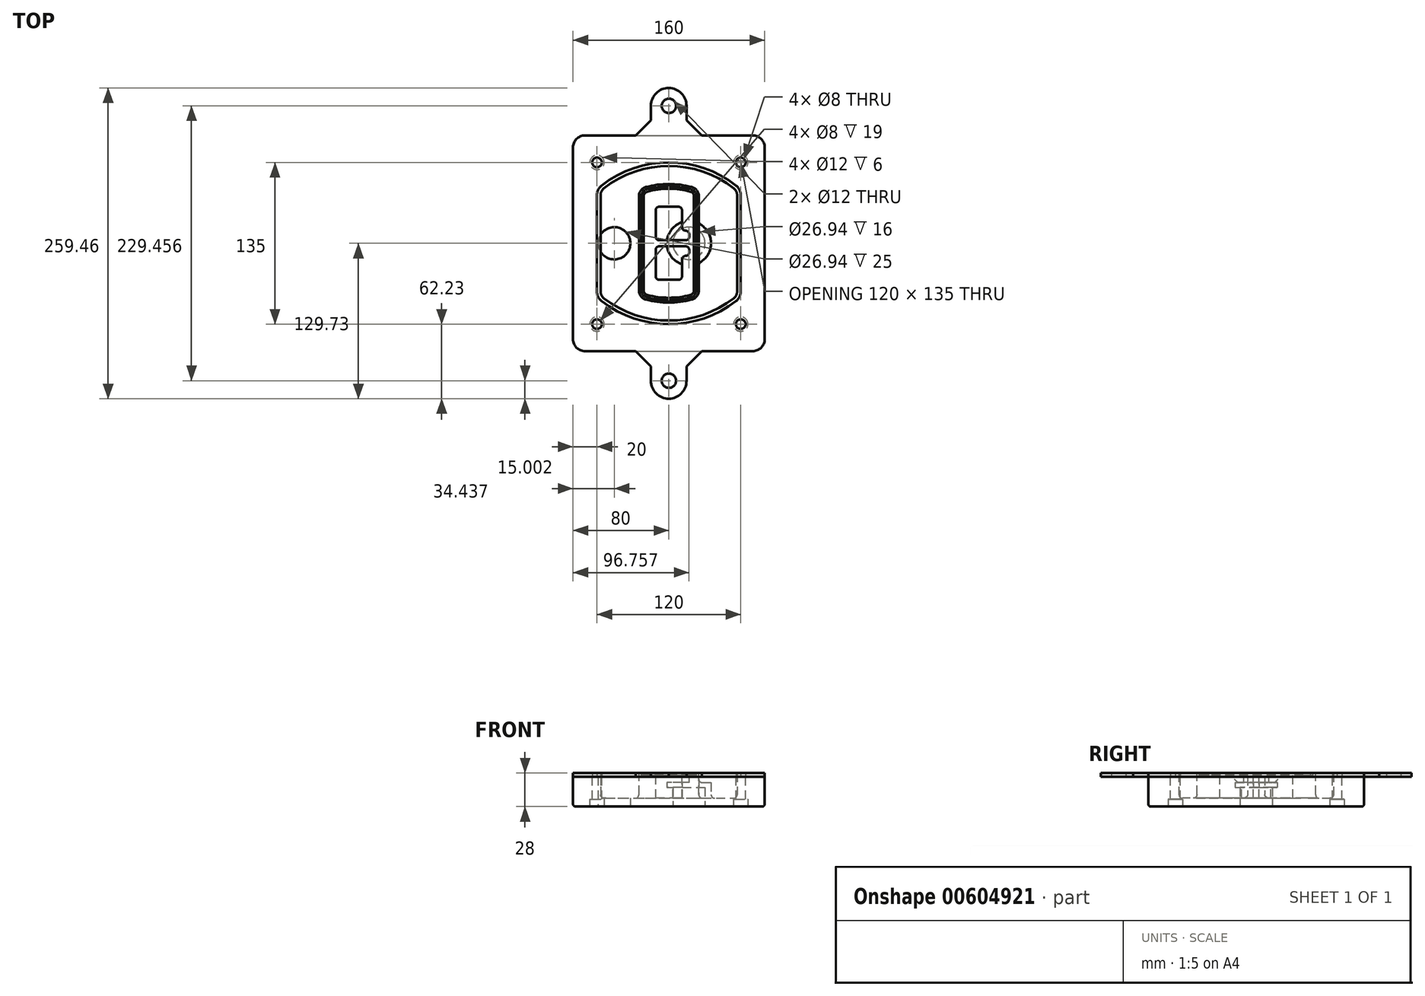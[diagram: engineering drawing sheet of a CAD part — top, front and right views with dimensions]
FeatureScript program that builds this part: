
annotation { "Feature Type Name" : "Feature", "Feature Type Description" : "" }
export const myFeature = defineFeature(function(context is Context, id is Id, definition is map)
    precondition{}
    {
        {
            var Q0;
            Q0=qCreatedBy(makeId("Top.planeOp"),FACE);
            var sketch = newSketch(context, id + "F0", { "sketchPlane" : qUnion([Q0])});
            skPoint(sketch, "E0.rect.middle", {"position": v(0, 0) * mm});
            skLineSegment(sketch, "E1.bottom", {"start": v(-70, -90) * mm, "end": v(70, -90) * mm});
            skLineSegment(sketch, "E1.top", {"start": v(-70, 90) * mm, "end": v(70, 90) * mm});
            skLineSegment(sketch, "E1.left", {"start": v(-80, -80) * mm, "end": v(-80, 80) * mm});
            skLineSegment(sketch, "E1.right", {"start": v(80, -80) * mm, "end": v(80, 80) * mm});
            skLineSegment(sketch, "E2", {"start": v(-80, 90) * mm, "end": v(80, -90) * mm, "construction": true});
            skLineSegment(sketch, "E3", {"start": v(80, 90) * mm, "end": v(-80, -90) * mm, "construction": true});
            skCircle(sketch, "E4", {"center": v(-60, 67.5) * mm, "radius": 4 * mm});
            skCircle(sketch, "E5", {"center": v(60, 67.5) * mm, "radius": 4 * mm});
            skCircle(sketch, "E6", {"center": v(60, -67.5) * mm, "radius": 4 * mm});
            skCircle(sketch, "E7", {"center": v(-60, -67.5) * mm, "radius": 4 * mm});
            skLineSegment(sketch, "E8", {"start": v(-60, 67.5) * mm, "end": v(60, 67.5) * mm, "construction": true});
            skLineSegment(sketch, "E9", {"start": v(60, 67.5) * mm, "end": v(60, -67.5) * mm, "construction": true});
            skLineSegment(sketch, "E10", {"start": v(60, -67.5) * mm, "end": v(-60, -67.5) * mm, "construction": true});
            skLineSegment(sketch, "E11", {"start": v(-60, -67.5) * mm, "end": v(-60, 67.5) * mm, "construction": true});
            skLineSegment(sketch, "E12", {"start": v(-60, 40.3) * mm, "end": v(-60, -40.3) * mm});
            skLineSegment(sketch, "E13", {"start": v(60, 40.3) * mm, "end": v(60, -40.3) * mm});
            skArc(sketch, "E14", {"start": v(56.15, 48.18) * mm, "mid": v(0, 67.5) * mm, "end": v(-56.15, 48.18) * mm});
            skArc(sketch, "E15", {"start": v(-56.15, -48.18) * mm, "mid": v(0, -67.5) * mm, "end": v(56.15, -48.18) * mm});
            skLineSegment(sketch, "E16", {"start": v(-60, 0) * mm, "end": v(60, 0) * mm, "construction": true});
            skPoint(sketch, "E17.visualSharp", {"position": v(-60, -45) * mm});
            skArc(sketch, "E17.filletArc", {"start": v(-60, -40.3) * mm, "mid": v(-58.99, -44.68) * mm, "end": v(-56.15, -48.18) * mm});
            skPoint(sketch, "E18.visualSharp", {"position": v(-60, 45) * mm});
            skArc(sketch, "E18.filletArc", {"start": v(-56.15, 48.18) * mm, "mid": v(-58.99, 44.68) * mm, "end": v(-60, 40.3) * mm});
            skPoint(sketch, "E19.visualSharp", {"position": v(60, 45) * mm});
            skArc(sketch, "E19.filletArc", {"start": v(60, 40.3) * mm, "mid": v(58.99, 44.68) * mm, "end": v(56.15, 48.18) * mm});
            skPoint(sketch, "E20.visualSharp", {"position": v(60, -45) * mm});
            skArc(sketch, "E20.filletArc", {"start": v(56.15, -48.18) * mm, "mid": v(58.99, -44.68) * mm, "end": v(60, -40.3) * mm});
            skPoint(sketch, "E21.visualSharp", {"position": v(-80, 90) * mm});
            skArc(sketch, "E21.filletArc", {"start": v(-70, 90) * mm, "mid": v(-77.07, 87.07) * mm, "end": v(-80, 80) * mm});
            skPoint(sketch, "E22.visualSharp", {"position": v(80, 90) * mm});
            skArc(sketch, "E22.filletArc", {"start": v(80, 80) * mm, "mid": v(77.07, 87.07) * mm, "end": v(70, 90) * mm});
            skPoint(sketch, "E23.visualSharp", {"position": v(80, -90) * mm});
            skArc(sketch, "E23.filletArc", {"start": v(70, -90) * mm, "mid": v(77.07, -87.07) * mm, "end": v(80, -80) * mm});
            skPoint(sketch, "E24.visualSharp", {"position": v(-80, -90) * mm});
            skArc(sketch, "E24.filletArc", {"start": v(-80, -80) * mm, "mid": v(-77.07, -87.07) * mm, "end": v(-70, -90) * mm});
            skArc(sketch, "E25.0", {"start": v(57, 40.3) * mm, "mid": v(56.3, 43.36) * mm, "end": v(54.3, 45.81) * mm});
            skLineSegment(sketch, "E25.1", {"start": v(57, 40.3) * mm, "end": v(57, -40.3) * mm});
            skArc(sketch, "E25.2", {"start": v(54.3, -45.81) * mm, "mid": v(56.3, -43.36) * mm, "end": v(57, -40.3) * mm});
            skArc(sketch, "E25.3", {"start": v(-54.3, -45.81) * mm, "mid": v(0, -64.5) * mm, "end": v(54.3, -45.81) * mm});
            skArc(sketch, "E25.4", {"start": v(-57, -40.3) * mm, "mid": v(-56.3, -43.36) * mm, "end": v(-54.3, -45.81) * mm});
            skArc(sketch, "E25.5", {"start": v(54.3, 45.81) * mm, "mid": v(0, 64.5) * mm, "end": v(-54.3, 45.81) * mm});
            skLineSegment(sketch, "E25.6", {"start": v(-57, 40.3) * mm, "end": v(-57, -40.3) * mm});
            skArc(sketch, "E25.7", {"start": v(-54.3, 45.81) * mm, "mid": v(-56.3, 43.36) * mm, "end": v(-57, 40.3) * mm});
            skArc(sketch, "E26.0", {"start": v(-58.62, 51.33) * mm, "mid": v(-62.58, 46.43) * mm, "end": v(-64, 40.3) * mm});
            skArc(sketch, "E26.1", {"start": v(58.62, 51.33) * mm, "mid": v(0, 71.5) * mm, "end": v(-58.62, 51.33) * mm});
            skArc(sketch, "E26.2", {"start": v(64, 40.3) * mm, "mid": v(62.58, 46.43) * mm, "end": v(58.62, 51.33) * mm});
            skLineSegment(sketch, "E26.3", {"start": v(64, 40.3) * mm, "end": v(64, -40.3) * mm});
            skArc(sketch, "E26.4", {"start": v(58.62, -51.33) * mm, "mid": v(62.58, -46.43) * mm, "end": v(64, -40.3) * mm});
            skLineSegment(sketch, "E26.5", {"start": v(-64, 40.3) * mm, "end": v(-64, -40.3) * mm});
            skArc(sketch, "E26.6", {"start": v(-58.62, -51.33) * mm, "mid": v(0, -71.5) * mm, "end": v(58.62, -51.33) * mm});
            skArc(sketch, "E26.7", {"start": v(-64, -40.3) * mm, "mid": v(-62.58, -46.43) * mm, "end": v(-58.62, -51.33) * mm});
            skSolve(sketch);
        }
        {
            var Q0;
            Q0=makeQuery(id+"F0.imprint","IMPRINT",FACE,{"disambiguationData":[TD([[makeQuery(id+"F0.imprint","IMPRINT",EDGE,{"derivedFrom":sQuery(id+"F0.wireOp",EDGE,"E1.bottom")}),1.0]])]});
            var Q1;
            Q1=makeQuery(id+"F0.imprint","IMPRINT",FACE,{"disambiguationData":[TD([[makeQuery(id+"F0.imprint","IMPRINT",EDGE,{"derivedFrom":sQuery(id+"F0.wireOp",EDGE,"E12")}),1.0]])]});
            var Q2;
            Q2=makeQuery(id+"F0.imprint","IMPRINT",FACE,{"disambiguationData":[TD([[makeQuery(id+"F0.imprint","IMPRINT",EDGE,{"derivedFrom":sQuery(id+"F0.wireOp",EDGE,"E25.0")}),1.0]])]});
            var Q3;
            Q3=makeQuery(id+"F0.imprint","IMPRINT",FACE,{"disambiguationData":[TD([[makeQuery(id+"F0.imprint","IMPRINT",EDGE,{"derivedFrom":sQuery(id+"F0.wireOp",EDGE,"E12")}),-1.0]])]});
            extrude(context, id + "F1", {"entities" : qUnion([Q0, Q1, Q2, Q3]), "oppositeDirection" : true, "depth" : 25 * mm});
        }
        {
            var Q0;
            Q0=makeQuery(id+"F0.imprint","IMPRINT",FACE,{"disambiguationData":[TD([[makeQuery(id+"F0.imprint","IMPRINT",EDGE,{"derivedFrom":sQuery(id+"F0.wireOp",EDGE,"E12")}),1.0]])]});
            extrude(context, id + "F2", {"entities" : qUnion([Q0]), "operationType" : NewBodyOperationType.ADD, "depth" : 3 * mm});
        }
        {
            var Q0;
            Q0=makeQuery(id+"F0.imprint","IMPRINT",FACE,{"disambiguationData":[TD([[makeQuery(id+"F0.imprint","IMPRINT",EDGE,{"derivedFrom":sQuery(id+"F0.wireOp",EDGE,"E25.0")}),1.0]])]});
            extrude(context, id + "F3", {"entities" : qUnion([Q0]), "operationType" : NewBodyOperationType.REMOVE, "oppositeDirection" : true, "depth" : 18 * mm});
        }
        {
            var Q0;
            Q0=makeQuery(id+"F2.opExtrude","CAP_FACE",FACE,{"disambiguationData":[OSD([sQuery(id+"F0.wireOp",EDGE,"E12"),sQuery(id+"F0.wireOp",EDGE,"E13"),sQuery(id+"F0.wireOp",EDGE,"E14"),sQuery(id+"F0.wireOp",EDGE,"E15"),sQuery(id+"F0.wireOp",EDGE,"E17.filletArc"),sQuery(id+"F0.wireOp",EDGE,"E18.filletArc"),sQuery(id+"F0.wireOp",EDGE,"E19.filletArc"),sQuery(id+"F0.wireOp",EDGE,"E20.filletArc"),sQuery(id+"F0.wireOp",EDGE,"E25.0"),sQuery(id+"F0.wireOp",EDGE,"E25.1"),sQuery(id+"F0.wireOp",EDGE,"E25.2"),sQuery(id+"F0.wireOp",EDGE,"E25.3"),sQuery(id+"F0.wireOp",EDGE,"E25.4"),sQuery(id+"F0.wireOp",EDGE,"E25.5"),sQuery(id+"F0.wireOp",EDGE,"E25.6"),sQuery(id+"F0.wireOp",EDGE,"E25.7")])],"isStart":false});
            var sketch = newSketch(context, id + "F4", { "sketchPlane" : qUnion([Q0])});
            skArc(sketch, "E27.0", {"start": v(-19.08, -46.97) * mm, "mid": v(0, -49.5) * mm, "end": v(19.08, -46.97) * mm});
            skArc(sketch, "E28.0", {"start": v(19.08, 46.97) * mm, "mid": v(0, 49.5) * mm, "end": v(-19.08, 46.97) * mm});
            skLineSegment(sketch, "E29", {"start": v(-25, 39.25) * mm, "end": v(-25, -39.25) * mm});
            skLineSegment(sketch, "E30", {"start": v(25, 39.25) * mm, "end": v(25, -39.25) * mm});
            skLineSegment(sketch, "E31", {"start": v(-25, 45.1) * mm, "end": v(25, 45.1) * mm, "construction": true});
            skLineSegment(sketch, "E32", {"start": v(-25, -45.1) * mm, "end": v(25, -45.1) * mm, "construction": true});
            skPoint(sketch, "E33.visualSharp", {"position": v(-25, 45.1) * mm});
            skArc(sketch, "E33.filletArc", {"start": v(-19.08, 46.97) * mm, "mid": v(-23.35, 44.11) * mm, "end": v(-25, 39.25) * mm});
            skPoint(sketch, "E34.visualSharp", {"position": v(25, 45.1) * mm});
            skArc(sketch, "E34.filletArc", {"start": v(25, 39.25) * mm, "mid": v(23.35, 44.11) * mm, "end": v(19.08, 46.97) * mm});
            skPoint(sketch, "E35.visualSharp", {"position": v(25, -45.1) * mm});
            skArc(sketch, "E35.filletArc", {"start": v(19.08, -46.97) * mm, "mid": v(23.35, -44.11) * mm, "end": v(25, -39.25) * mm});
            skPoint(sketch, "E36.visualSharp", {"position": v(-25, -45.1) * mm});
            skArc(sketch, "E36.filletArc", {"start": v(-25, -39.25) * mm, "mid": v(-23.35, -44.11) * mm, "end": v(-19.08, -46.97) * mm});
            skArc(sketch, "E37.0", {"start": v(54.3, 45.81) * mm, "mid": v(0, 64.5) * mm, "end": v(-54.3, 45.81) * mm});
            skArc(sketch, "E37.1", {"start": v(-54.3, 45.81) * mm, "mid": v(-56.3, 43.36) * mm, "end": v(-57, 40.3) * mm});
            skLineSegment(sketch, "E37.2", {"start": v(-57, 40.3) * mm, "end": v(-57, -40.3) * mm});
            skArc(sketch, "E37.3", {"start": v(-57, -40.3) * mm, "mid": v(-56.3, -43.36) * mm, "end": v(-54.3, -45.81) * mm});
            skArc(sketch, "E37.4", {"start": v(-54.3, -45.81) * mm, "mid": v(0, -64.5) * mm, "end": v(54.3, -45.81) * mm});
            skArc(sketch, "E37.5", {"start": v(54.3, -45.81) * mm, "mid": v(56.3, -43.36) * mm, "end": v(57, -40.3) * mm});
            skLineSegment(sketch, "E37.6", {"start": v(57, 40.3) * mm, "end": v(57, -40.3) * mm});
            skArc(sketch, "E37.7", {"start": v(57, 40.3) * mm, "mid": v(56.3, 43.36) * mm, "end": v(54.3, 45.81) * mm});
            skLineSegment(sketch, "E38.0", {"start": v(23, 39.25) * mm, "end": v(23, -39.25) * mm});
            skArc(sketch, "E38.1", {"start": v(18.56, -45.04) * mm, "mid": v(21.76, -42.9) * mm, "end": v(23, -39.25) * mm});
            skArc(sketch, "E38.2", {"start": v(-18.56, -45.04) * mm, "mid": v(0, -47.5) * mm, "end": v(18.56, -45.04) * mm});
            skArc(sketch, "E38.3", {"start": v(-23, -39.25) * mm, "mid": v(-21.76, -42.9) * mm, "end": v(-18.56, -45.04) * mm});
            skLineSegment(sketch, "E38.4", {"start": v(-23, 39.25) * mm, "end": v(-23, -39.25) * mm});
            skArc(sketch, "E38.5", {"start": v(23, 39.25) * mm, "mid": v(21.76, 42.9) * mm, "end": v(18.56, 45.04) * mm});
            skArc(sketch, "E38.6", {"start": v(-18.56, 45.04) * mm, "mid": v(-21.76, 42.9) * mm, "end": v(-23, 39.25) * mm});
            skArc(sketch, "E38.7", {"start": v(18.56, 45.04) * mm, "mid": v(0, 47.5) * mm, "end": v(-18.56, 45.04) * mm});
            skArc(sketch, "E39.0", {"start": v(21, 39.25) * mm, "mid": v(20.18, 41.68) * mm, "end": v(18.04, 43.1) * mm});
            skLineSegment(sketch, "E39.1", {"start": v(21, 39.25) * mm, "end": v(21, -39.25) * mm});
            skArc(sketch, "E39.2", {"start": v(18.04, -43.1) * mm, "mid": v(20.18, -41.68) * mm, "end": v(21, -39.25) * mm});
            skArc(sketch, "E39.3", {"start": v(-18.04, -43.1) * mm, "mid": v(0, -45.5) * mm, "end": v(18.04, -43.1) * mm});
            skArc(sketch, "E39.4", {"start": v(-21, -39.25) * mm, "mid": v(-20.18, -41.68) * mm, "end": v(-18.04, -43.1) * mm});
            skArc(sketch, "E39.5", {"start": v(18.04, 43.1) * mm, "mid": v(0, 45.5) * mm, "end": v(-18.04, 43.1) * mm});
            skLineSegment(sketch, "E39.6", {"start": v(-21, 39.25) * mm, "end": v(-21, -39.25) * mm});
            skArc(sketch, "E39.7", {"start": v(-18.04, 43.1) * mm, "mid": v(-20.18, 41.68) * mm, "end": v(-21, 39.25) * mm});
            skLineSegment(sketch, "E40", {"start": v(-25, 0) * mm, "end": v(25, 0) * mm, "construction": true});
            skLineSegment(sketch, "E41", {"start": v(-11, 5.5) * mm, "end": v(-11, 27.5) * mm});
            skLineSegment(sketch, "E42", {"start": v(-8, 30.5) * mm, "end": v(8, 30.5) * mm});
            skLineSegment(sketch, "E43", {"start": v(11, 27.5) * mm, "end": v(11, 13.5) * mm});
            skLineSegment(sketch, "E44", {"start": v(14, 10.5) * mm, "end": v(14, 10.5) * mm});
            skLineSegment(sketch, "E45", {"start": v(17, 7.5) * mm, "end": v(17, 5.5) * mm});
            skLineSegment(sketch, "E46", {"start": v(14, 2.5) * mm, "end": v(-8, 2.5) * mm});
            skPoint(sketch, "E47.visualSharp", {"position": v(-11, 30.5) * mm});
            skArc(sketch, "E47.filletArc", {"start": v(-8, 30.5) * mm, "mid": v(-10.12, 29.62) * mm, "end": v(-11, 27.5) * mm});
            skPoint(sketch, "E48.visualSharp", {"position": v(11, 30.5) * mm});
            skArc(sketch, "E48.filletArc", {"start": v(11, 27.5) * mm, "mid": v(10.12, 29.62) * mm, "end": v(8, 30.5) * mm});
            skPoint(sketch, "E49.visualSharp", {"position": v(11, 10.5) * mm});
            skArc(sketch, "E49.filletArc", {"start": v(11, 13.5) * mm, "mid": v(11.88, 11.38) * mm, "end": v(14, 10.5) * mm});
            skPoint(sketch, "E50.visualSharp", {"position": v(17, 10.5) * mm});
            skArc(sketch, "E50.filletArc", {"start": v(17, 7.5) * mm, "mid": v(16.12, 9.62) * mm, "end": v(14, 10.5) * mm});
            skPoint(sketch, "E51.visualSharp", {"position": v(17, 2.5) * mm});
            skArc(sketch, "E51.filletArc", {"start": v(14, 2.5) * mm, "mid": v(16.12, 3.38) * mm, "end": v(17, 5.5) * mm});
            skPoint(sketch, "E52.visualSharp", {"position": v(-11, 2.5) * mm});
            skArc(sketch, "E52.filletArc", {"start": v(-11, 5.5) * mm, "mid": v(-10.12, 3.38) * mm, "end": v(-8, 2.5) * mm});
            skLineSegment(sketch, "E53.0.MirrorCS", {"start": v(14, -2.5) * mm, "end": v(-8, -2.5) * mm});
            skArc(sketch, "E54.0.MirrorCS", {"start": v(-11, -5.5) * mm, "mid": v(-10.12, -3.38) * mm, "end": v(-8, -2.5) * mm});
            skLineSegment(sketch, "E55.0.MirrorCS", {"start": v(-11, -5.5) * mm, "end": v(-11, -27.5) * mm});
            skArc(sketch, "E56.0.MirrorCS", {"start": v(-8, -30.5) * mm, "mid": v(-10.12, -29.62) * mm, "end": v(-11, -27.5) * mm});
            skLineSegment(sketch, "E57.0.MirrorCS", {"start": v(-8, -30.5) * mm, "end": v(8, -30.5) * mm});
            skArc(sketch, "E58.0.MirrorCS", {"start": v(11, -27.5) * mm, "mid": v(10.12, -29.62) * mm, "end": v(8, -30.5) * mm});
            skLineSegment(sketch, "E59.0.MirrorCS", {"start": v(11, -27.5) * mm, "end": v(11, -13.5) * mm});
            skArc(sketch, "E60.0.MirrorCS", {"start": v(11, -13.5) * mm, "mid": v(11.88, -11.38) * mm, "end": v(14, -10.5) * mm});
            skArc(sketch, "E61.0.MirrorCS", {"start": v(17, -7.5) * mm, "mid": v(16.12, -9.62) * mm, "end": v(14, -10.5) * mm});
            skLineSegment(sketch, "E62.0.MirrorCS", {"start": v(17, -7.5) * mm, "end": v(17, -5.5) * mm});
            skArc(sketch, "E63.0.MirrorCS", {"start": v(14, -2.5) * mm, "mid": v(16.12, -3.38) * mm, "end": v(17, -5.5) * mm});
            skSolve(sketch);
        }
        {
            var Q0;
            Q0=makeQuery(id+"F4.imprint","IMPRINT",FACE,{"disambiguationData":[TD([[makeQuery(id+"F4.imprint","IMPRINT",EDGE,{"derivedFrom":sQuery(id+"F4.wireOp",EDGE,"E27.0")}),1.0]])]});
            var Q1;
            Q1=makeQuery(id+"F4.imprint","IMPRINT",FACE,{"disambiguationData":[TD([[makeQuery(id+"F4.imprint","IMPRINT",EDGE,{"derivedFrom":sQuery(id+"F4.wireOp",EDGE,"E38.0")}),-1.0]])]});
            var Q2;
            Q2=makeQuery(id+"F4.imprint","IMPRINT",FACE,{"disambiguationData":[TD([[makeQuery(id+"F4.imprint","IMPRINT",EDGE,{"derivedFrom":sQuery(id+"F4.wireOp",EDGE,"E39.0")}),1.0]])]});
            extrude(context, id + "F5", {"entities" : qUnion([Q0, Q1, Q2]), "operationType" : NewBodyOperationType.ADD, "endBound" : BoundingType.UP_TO_NEXT, "oppositeDirection" : true, "depth" : 25 * mm});
        }
        {
            var Q0;
            Q0=makeQuery(id+"F4.imprint","IMPRINT",FACE,{"disambiguationData":[TD([[makeQuery(id+"F4.imprint","IMPRINT",EDGE,{"derivedFrom":sQuery(id+"F4.wireOp",EDGE,"E38.0")}),-1.0]])]});
            extrude(context, id + "F6", {"entities" : qUnion([Q0]), "operationType" : NewBodyOperationType.REMOVE, "oppositeDirection" : true, "depth" : 2 * mm});
        }
        {
            var Q0;
            Q0=makeQuery(id+"F1.opExtrude","CAP_FACE",FACE,{"disambiguationData":[OSD([sQuery(id+"F0.wireOp",EDGE,"E1.bottom"),sQuery(id+"F0.wireOp",EDGE,"E1.top"),sQuery(id+"F0.wireOp",EDGE,"E1.left"),sQuery(id+"F0.wireOp",EDGE,"E1.right"),sQuery(id+"F0.wireOp",EDGE,"E4"),sQuery(id+"F0.wireOp",EDGE,"E5"),sQuery(id+"F0.wireOp",EDGE,"E6"),sQuery(id+"F0.wireOp",EDGE,"E7"),sQuery(id+"F0.wireOp",EDGE,"E21.filletArc"),sQuery(id+"F0.wireOp",EDGE,"E22.filletArc"),sQuery(id+"F0.wireOp",EDGE,"E23.filletArc"),sQuery(id+"F0.wireOp",EDGE,"E24.filletArc")])],"isStart":false});
            var sketch = newSketch(context, id + "F7", { "sketchPlane" : qUnion([Q0])});
            skCircle(sketch, "E64", {"center": v(16.76, 0) * mm, "radius": 13.47 * mm});
            skCircle(sketch, "E65", {"center": v(-45.56, 0) * mm, "radius": 13.47 * mm});
            skLineSegment(sketch, "E66", {"start": v(80, 0) * mm, "end": v(-80, 0) * mm});
            skCircle(sketch, "E67", {"center": v(16.76, 0) * mm, "radius": 18.47 * mm});
            skCircle(sketch, "E68", {"center": v(60, -67.5) * mm, "radius": 6 * mm});
            skCircle(sketch, "E69", {"center": v(-60, -67.5) * mm, "radius": 6 * mm});
            skCircle(sketch, "E70", {"center": v(-60, 67.5) * mm, "radius": 6 * mm});
            skCircle(sketch, "E71", {"center": v(60, 67.5) * mm, "radius": 6 * mm});
            skSolve(sketch);
        }
        {
            var Q0;
            {var subQ1=sQuery(id+"F7.wireOp",EDGE,"E66");var subQ4=sQuery(id+"F7.wireOp",EDGE,"E64");var subQ6=makeQuery(id+"F7.imprint","INTERSECT",VERTEX,{"disambiguationData":[OD(0.0)],"derivedFrom":[subQ4,subQ1]});Q0=makeQuery(id+"F7.imprint","IMPRINT",FACE,{"disambiguationData":[TD([[makeQuery(id+"F7.imprint","IMPRINT",EDGE,{"disambiguationData":[TD([[subQ6,-1.0]])],"derivedFrom":subQ4}),-1.0]])]});}
            var Q1;
            {var subQ0=sQuery(id+"F7.wireOp",EDGE,"E66");var subQ1=sQuery(id+"F7.wireOp",EDGE,"E64");var subQ3=makeQuery(id+"F7.imprint","INTERSECT",VERTEX,{"disambiguationData":[OD(0.0)],"derivedFrom":[subQ1,subQ0]});Q1=makeQuery(id+"F7.imprint","IMPRINT",FACE,{"disambiguationData":[TD([[makeQuery(id+"F7.imprint","IMPRINT",EDGE,{"disambiguationData":[TD([[subQ3,-1.0]])],"derivedFrom":subQ1}),1.0]])]});}
            var Q2;
            {var subQ0=sQuery(id+"F7.wireOp",EDGE,"E66");var subQ1=sQuery(id+"F7.wireOp",EDGE,"E64");var subQ3=makeQuery(id+"F7.imprint","INTERSECT",VERTEX,{"disambiguationData":[OD(0.0)],"derivedFrom":[subQ1,subQ0]});Q2=makeQuery(id+"F7.imprint","IMPRINT",FACE,{"disambiguationData":[TD([[makeQuery(id+"F7.imprint","IMPRINT",EDGE,{"disambiguationData":[TD([[subQ3,1.0]])],"derivedFrom":subQ1}),1.0]])]});}
            var Q3;
            {var subQ1=sQuery(id+"F7.wireOp",EDGE,"E66");var subQ4=sQuery(id+"F7.wireOp",EDGE,"E64");var subQ6=makeQuery(id+"F7.imprint","INTERSECT",VERTEX,{"disambiguationData":[OD(0.0)],"derivedFrom":[subQ4,subQ1]});Q3=makeQuery(id+"F7.imprint","IMPRINT",FACE,{"disambiguationData":[TD([[makeQuery(id+"F7.imprint","IMPRINT",EDGE,{"disambiguationData":[TD([[subQ6,1.0]])],"derivedFrom":subQ4}),-1.0]])]});}
            extrude(context, id + "F8", {"entities" : qUnion([Q0, Q1, Q2, Q3]), "operationType" : NewBodyOperationType.ADD, "oppositeDirection" : true, "depth" : 20 * mm});
        }
        {
            var Q0;
            {var subQ0=sQuery(id+"F7.wireOp",EDGE,"E66");var subQ1=sQuery(id+"F7.wireOp",EDGE,"E64");var subQ3=makeQuery(id+"F7.imprint","INTERSECT",VERTEX,{"disambiguationData":[OD(0.0)],"derivedFrom":[subQ1,subQ0]});Q0=makeQuery(id+"F7.imprint","IMPRINT",FACE,{"disambiguationData":[TD([[makeQuery(id+"F7.imprint","IMPRINT",EDGE,{"disambiguationData":[TD([[subQ3,-1.0]])],"derivedFrom":subQ1}),1.0]])]});}
            var Q1;
            {var subQ0=sQuery(id+"F7.wireOp",EDGE,"E66");var subQ1=sQuery(id+"F7.wireOp",EDGE,"E64");var subQ3=makeQuery(id+"F7.imprint","INTERSECT",VERTEX,{"disambiguationData":[OD(0.0)],"derivedFrom":[subQ1,subQ0]});Q1=makeQuery(id+"F7.imprint","IMPRINT",FACE,{"disambiguationData":[TD([[makeQuery(id+"F7.imprint","IMPRINT",EDGE,{"disambiguationData":[TD([[subQ3,1.0]])],"derivedFrom":subQ1}),1.0]])]});}
            extrude(context, id + "F9", {"entities" : qUnion([Q0, Q1]), "operationType" : NewBodyOperationType.REMOVE, "oppositeDirection" : true, "depth" : 16 * mm});
        }
        {
            var Q0;
            {var subQ0=sQuery(id+"F7.wireOp",EDGE,"E66");var subQ1=sQuery(id+"F7.wireOp",EDGE,"E65");var subQ3=makeQuery(id+"F7.imprint","INTERSECT",VERTEX,{"disambiguationData":[OD(0.0)],"derivedFrom":[subQ1,subQ0]});Q0=makeQuery(id+"F7.imprint","IMPRINT",FACE,{"disambiguationData":[TD([[makeQuery(id+"F7.imprint","IMPRINT",EDGE,{"disambiguationData":[TD([[subQ3,-1.0]])],"derivedFrom":subQ1}),1.0]])]});}
            var Q1;
            {var subQ0=sQuery(id+"F7.wireOp",EDGE,"E66");var subQ1=sQuery(id+"F7.wireOp",EDGE,"E65");var subQ3=makeQuery(id+"F7.imprint","INTERSECT",VERTEX,{"disambiguationData":[OD(0.0)],"derivedFrom":[subQ1,subQ0]});Q1=makeQuery(id+"F7.imprint","IMPRINT",FACE,{"disambiguationData":[TD([[makeQuery(id+"F7.imprint","IMPRINT",EDGE,{"disambiguationData":[TD([[subQ3,1.0]])],"derivedFrom":subQ1}),1.0]])]});}
            extrude(context, id + "F10", {"entities" : qUnion([Q0, Q1]), "operationType" : NewBodyOperationType.REMOVE, "oppositeDirection" : true, "depth" : 25 * mm});
        }
        {
            var Q0;
            Q0=makeQuery(id+"F7.imprint","IMPRINT",FACE,{"disambiguationData":[TD([[makeQuery(id+"F7.imprint","IMPRINT",EDGE,{"derivedFrom":sQuery(id+"F7.wireOp",EDGE,"E68")}),1.0]])]});
            var Q1;
            Q1=makeQuery(id+"F7.imprint","IMPRINT",FACE,{"disambiguationData":[TD([[makeQuery(id+"F7.imprint","IMPRINT",EDGE,{"derivedFrom":makeQuery(id+"F1.opExtrude","CAP_EDGE",EDGE,{"disambiguationData":[OSD([sQuery(id+"F0.wireOp",EDGE,"E5")])],"isStart":false})}),-1.0]])]});
            var Q2;
            Q2=makeQuery(id+"F7.imprint","IMPRINT",FACE,{"disambiguationData":[TD([[makeQuery(id+"F7.imprint","IMPRINT",EDGE,{"derivedFrom":sQuery(id+"F7.wireOp",EDGE,"E69")}),1.0]])]});
            var Q3;
            Q3=makeQuery(id+"F7.imprint","IMPRINT",FACE,{"disambiguationData":[TD([[makeQuery(id+"F7.imprint","IMPRINT",EDGE,{"derivedFrom":makeQuery(id+"F1.opExtrude","CAP_EDGE",EDGE,{"disambiguationData":[OSD([sQuery(id+"F0.wireOp",EDGE,"E4")])],"isStart":false})}),-1.0]])]});
            var Q4;
            Q4=makeQuery(id+"F7.imprint","IMPRINT",FACE,{"disambiguationData":[TD([[makeQuery(id+"F7.imprint","IMPRINT",EDGE,{"derivedFrom":sQuery(id+"F7.wireOp",EDGE,"E70")}),1.0]])]});
            var Q5;
            Q5=makeQuery(id+"F7.imprint","IMPRINT",FACE,{"disambiguationData":[TD([[makeQuery(id+"F7.imprint","IMPRINT",EDGE,{"derivedFrom":makeQuery(id+"F1.opExtrude","CAP_EDGE",EDGE,{"disambiguationData":[OSD([sQuery(id+"F0.wireOp",EDGE,"E7")])],"isStart":false})}),-1.0]])]});
            var Q6;
            Q6=makeQuery(id+"F7.imprint","IMPRINT",FACE,{"disambiguationData":[TD([[makeQuery(id+"F7.imprint","IMPRINT",EDGE,{"derivedFrom":sQuery(id+"F7.wireOp",EDGE,"E71")}),1.0]])]});
            var Q7;
            Q7=makeQuery(id+"F7.imprint","IMPRINT",FACE,{"disambiguationData":[TD([[makeQuery(id+"F7.imprint","IMPRINT",EDGE,{"derivedFrom":makeQuery(id+"F1.opExtrude","CAP_EDGE",EDGE,{"disambiguationData":[OSD([sQuery(id+"F0.wireOp",EDGE,"E6")])],"isStart":false})}),-1.0]])]});
            extrude(context, id + "F11", {"entities" : qUnion([Q0, Q1, Q2, Q3, Q4, Q5, Q6, Q7]), "operationType" : NewBodyOperationType.REMOVE, "oppositeDirection" : true, "depth" : 6 * mm});
        }
        {
            var Q0;
            Q0=makeQuery(id+"F9.boolean.opBoolean","COPY",FACE,{"derivedFrom":makeQuery(id+"F9.opExtrude","CAP_FACE",FACE,{"disambiguationData":[OSD([sQuery(id+"F7.wireOp",EDGE,"E64")])],"isStart":false})});
            var sketch = newSketch(context, id + "F12", { "sketchPlane" : qUnion([Q0])});
            skArc(sketch, "E72.0", {"start": v(11, 17.55) * mm, "mid": v(2.57, 11.82) * mm, "end": v(-1.54, 2.5) * mm});
            skArc(sketch, "E72.1", {"start": v(-1.54, -2.5) * mm, "mid": v(2.57, -11.82) * mm, "end": v(11, -17.55) * mm});
            skLineSegment(sketch, "E73", {"start": v(-1.54, -2.5) * mm, "end": v(14, -2.5) * mm});
            skLineSegment(sketch, "E74.0", {"start": v(14, 2.5) * mm, "end": v(-1.54, 2.5) * mm});
            skArc(sketch, "E74.1", {"start": v(14, 2.5) * mm, "mid": v(16.12, 3.38) * mm, "end": v(17, 5.5) * mm});
            skLineSegment(sketch, "E74.2", {"start": v(17, 7.5) * mm, "end": v(17, 5.5) * mm});
            skArc(sketch, "E74.3", {"start": v(17, 7.5) * mm, "mid": v(16.12, 9.62) * mm, "end": v(14, 10.5) * mm});
            skArc(sketch, "E74.4", {"start": v(11, 13.5) * mm, "mid": v(11.88, 11.38) * mm, "end": v(14, 10.5) * mm});
            skLineSegment(sketch, "E74.5", {"start": v(11, 17.55) * mm, "end": v(11, 13.5) * mm});
            skLineSegment(sketch, "E74.7", {"start": v(14, -2.5) * mm, "end": v(-1.54, -2.5) * mm});
            skArc(sketch, "E74.8", {"start": v(14, -2.5) * mm, "mid": v(16.12, -3.38) * mm, "end": v(17, -5.5) * mm});
            skLineSegment(sketch, "E74.9", {"start": v(17, -7.5) * mm, "end": v(17, -5.5) * mm});
            skArc(sketch, "E74.10", {"start": v(17, -7.5) * mm, "mid": v(16.12, -9.62) * mm, "end": v(14, -10.5) * mm});
            skArc(sketch, "E74.11", {"start": v(11, -13.5) * mm, "mid": v(11.88, -11.38) * mm, "end": v(14, -10.5) * mm});
            skLineSegment(sketch, "E74.12", {"start": v(11, -17.55) * mm, "end": v(11, -13.5) * mm});
            skPoint(sketch, "E75.orphan", {"position": v(11, -27.5) * mm});
            skPoint(sketch, "E76.orphan", {"position": v(-8, -2.5) * mm});
            skPoint(sketch, "E77.orphan", {"position": v(-8, 2.5) * mm});
            skPoint(sketch, "E78.orphan", {"position": v(11, 27.5) * mm});
            skSolve(sketch);
        }
        {
            var Q0;
            {var subQ7=sQuery(id+"F12.wireOp",EDGE,"E72.0");var subQ14=sQuery(id+"F12.wireOp",EDGE,"E72.1");var subQ16=sQuery(id+"F12.wireOp",EDGE,"E74.1");var subQ18=sQuery(id+"F12.wireOp",EDGE,"E74.8");Q0=qUnion([makeQuery(id+"F12.imprint","IMPRINT",FACE,{"disambiguationData":[TD([[makeQuery(id+"F12.imprint","IMPRINT",EDGE,{"derivedFrom":subQ7}),1.0]])]}),makeQuery(id+"F12.imprint","IMPRINT",FACE,{"disambiguationData":[TD([[makeQuery(id+"F12.imprint","IMPRINT",EDGE,{"derivedFrom":subQ14}),1.0]])]}),makeQuery(id+"F12.imprint","IMPRINT",FACE,{"disambiguationData":[TD([[makeQuery(id+"F12.imprint","IMPRINT",EDGE,{"derivedFrom":subQ16}),1.0]])]}),makeQuery(id+"F12.imprint","IMPRINT",FACE,{"disambiguationData":[TD([[makeQuery(id+"F12.imprint","IMPRINT",EDGE,{"derivedFrom":subQ18}),-1.0]])]})]);}
            var Q1;
            Q1=makeQuery(id+"F5.boolean.opBoolean","SPLIT",FACE,{"disambiguationData":[TD([makeQuery(id+"F5.opExtrude","SWEPT_FACE",FACE,{"disambiguationData":[OSD([sQuery(id+"F4.wireOp",EDGE,"E41")])]})])],"derivedFrom":makeQuery(id+"F3.boolean.opBoolean","COPY",FACE,{"derivedFrom":makeQuery(id+"F3.opExtrude","CAP_FACE",FACE,{"disambiguationData":[OSD([sQuery(id+"F0.wireOp",EDGE,"E25.0"),sQuery(id+"F0.wireOp",EDGE,"E25.1"),sQuery(id+"F0.wireOp",EDGE,"E25.2"),sQuery(id+"F0.wireOp",EDGE,"E25.3"),sQuery(id+"F0.wireOp",EDGE,"E25.4"),sQuery(id+"F0.wireOp",EDGE,"E25.5"),sQuery(id+"F0.wireOp",EDGE,"E25.6"),sQuery(id+"F0.wireOp",EDGE,"E25.7")])],"isStart":false})})});
            extrude(context, id + "F13", {"entities" : qUnion([Q0]), "operationType" : NewBodyOperationType.REMOVE, "endBound" : BoundingType.UP_TO_SURFACE, "endBoundEntityFace" : qUnion([Q1]), "depth" : 25 * mm});
        }
        {
            var Q0;
            Q0=makeQuery(id+"F3.boolean.opBoolean","COPY",EDGE,{"derivedFrom":makeQuery(id+"F3.opExtrude","CAP_EDGE",EDGE,{"disambiguationData":[OSD([sQuery(id+"F0.wireOp",EDGE,"E25.6")])],"isStart":false})});
            var Q1;
            Q1=makeQuery(id+"F8.boolean.opBoolean","INTERSECT",EDGE,{"derivedFrom":[makeQuery(id+"F5.opExtrude","SWEPT_FACE",FACE,{"disambiguationData":[OSD([sQuery(id+"F4.wireOp",EDGE,"E30")])]}),makeQuery(id+"F8.opExtrude","CAP_FACE",FACE,{"disambiguationData":[OSD([sQuery(id+"F7.wireOp",EDGE,"E67")])],"isStart":false})]});
            var Q2;
            Q2=makeQuery(id+"F8.boolean.opBoolean","INTERSECT",EDGE,{"disambiguationData":[OD(1.0)],"derivedFrom":[makeQuery(id+"F5.opExtrude","SWEPT_FACE",FACE,{"disambiguationData":[OSD([sQuery(id+"F4.wireOp",EDGE,"E30")])]}),makeQuery(id+"F8.opExtrude","SWEPT_FACE",FACE,{"disambiguationData":[OSD([sQuery(id+"F7.wireOp",EDGE,"E67")])]})]});
            var Q3;
            {var subQ0=sQuery(id+"F4.wireOp",EDGE,"E30");Q3=makeQuery(id+"F8.boolean.opBoolean","SPLIT",EDGE,{"disambiguationData":[TD([makeQuery(id+"F5.opExtrude","SWEPT_FACE",FACE,{"disambiguationData":[OSD([sQuery(id+"F4.wireOp",EDGE,"E35.filletArc")])]})])],"derivedFrom":makeQuery(id+"F5.opExtrude","CAP_EDGE",EDGE,{"disambiguationData":[OSD([subQ0])],"isStart":false})});}
            var Q4;
            {var subQ0=sQuery(id+"F0.wireOp",EDGE,"E25.7");var subQ1=sQuery(id+"F0.wireOp",EDGE,"E25.1");var subQ2=sQuery(id+"F0.wireOp",EDGE,"E25.6");var subQ3=sQuery(id+"F0.wireOp",EDGE,"E25.5");var subQ4=sQuery(id+"F0.wireOp",EDGE,"E25.4");var subQ5=sQuery(id+"F0.wireOp",EDGE,"E25.0");var subQ6=sQuery(id+"F0.wireOp",EDGE,"E25.2");var subQ7=sQuery(id+"F0.wireOp",EDGE,"E25.3");Q4=makeQuery(id+"F8.boolean.opBoolean","INTERSECT",EDGE,{"derivedFrom":[makeQuery(id+"F5.boolean.opBoolean","SPLIT",FACE,{"disambiguationData":[TD([makeQuery(id+"F2.opExtrude","SWEPT_FACE",FACE,{"disambiguationData":[OSD([subQ5])]})])],"derivedFrom":makeQuery(id+"F3.boolean.opBoolean","COPY",FACE,{"derivedFrom":makeQuery(id+"F3.opExtrude","CAP_FACE",FACE,{"disambiguationData":[OSD([subQ5,subQ1,subQ6,subQ7,subQ4,subQ3,subQ2,subQ0])],"isStart":false})})}),makeQuery(id+"F8.opExtrude","SWEPT_FACE",FACE,{"disambiguationData":[OSD([sQuery(id+"F7.wireOp",EDGE,"E67")])]})]});}
            var Q5;
            Q5=makeQuery(id+"F8.boolean.opBoolean","INTERSECT",EDGE,{"disambiguationData":[OD(0.0)],"derivedFrom":[makeQuery(id+"F5.opExtrude","SWEPT_FACE",FACE,{"disambiguationData":[OSD([sQuery(id+"F4.wireOp",EDGE,"E30")])]}),makeQuery(id+"F8.opExtrude","SWEPT_FACE",FACE,{"disambiguationData":[OSD([sQuery(id+"F7.wireOp",EDGE,"E67")])]})]});
            fillet(context, id + "F14", {"entities" : qUnion([Q0, Q1, Q2, Q3, Q4, Q5]), "radius" : 3 * mm, "tangentPropagation" : true, "allowEdgeOverflow" : false});
        }
        {
            var Q0;
            Q0=makeQuery(id+"F1.opExtrude","CAP_EDGE",EDGE,{"disambiguationData":[OSD([sQuery(id+"F0.wireOp",EDGE,"E1.bottom")])],"isStart":false});
            fillet(context, id + "F15", {"entities" : qUnion([Q0]), "radius" : 2 * mm, "tangentPropagation" : true, "allowEdgeOverflow" : false});
        }
        {
            var Q0;
            {var subQ0=sQuery(id+"F0.wireOp",EDGE,"E21.filletArc");var subQ1=sQuery(id+"F0.wireOp",EDGE,"E7");var subQ2=sQuery(id+"F0.wireOp",EDGE,"E6");var subQ3=sQuery(id+"F0.wireOp",EDGE,"E5");var subQ4=sQuery(id+"F0.wireOp",EDGE,"E4");var subQ5=sQuery(id+"F0.wireOp",EDGE,"E22.filletArc");var subQ6=sQuery(id+"F0.wireOp",EDGE,"E1.bottom");var subQ7=sQuery(id+"F0.wireOp",EDGE,"E1.right");var subQ8=sQuery(id+"F0.wireOp",EDGE,"E1.top");var subQ9=sQuery(id+"F0.wireOp",EDGE,"E1.left");var subQ10=sQuery(id+"F0.wireOp",EDGE,"E23.filletArc");var subQ11=sQuery(id+"F0.wireOp",EDGE,"E24.filletArc");Q0=makeQuery(id+"F2.boolean.opBoolean","SPLIT",FACE,{"disambiguationData":[TD([makeQuery(id+"F1.opExtrude","SWEPT_FACE",FACE,{"disambiguationData":[OSD([subQ6])]})])],"derivedFrom":makeQuery(id+"F1.opExtrude","CAP_FACE",FACE,{"disambiguationData":[OSD([subQ6,subQ8,subQ9,subQ7,subQ4,subQ3,subQ2,subQ1,subQ0,subQ5,subQ10,subQ11])],"isStart":true})});}
            var sketch = newSketch(context, id + "F16", { "sketchPlane" : qUnion([Q0])});
            skLineSegment(sketch, "E79", {"start": v(27.46, 90) * mm, "end": v(14.73, 102.73) * mm});
            skLineSegment(sketch, "E80", {"start": v(-27.73, 90) * mm, "end": v(-15, 102.73) * mm});
            skLineSegment(sketch, "E81", {"start": v(-15, 102.73) * mm, "end": v(-15, 114.73) * mm});
            skLineSegment(sketch, "E82", {"start": v(14.73, 102.73) * mm, "end": v(14.73, 114.73) * mm});
            skArc(sketch, "E83", {"start": v(0, 129.73) * mm, "mid": v(-10.6, 125.33) * mm, "end": v(-15, 114.73) * mm});
            skArc(sketch, "E84", {"start": v(14.73, 114.73) * mm, "mid": v(10.43, 125.24) * mm, "end": v(0, 129.73) * mm});
            skCircle(sketch, "E85", {"center": v(0, 114.73) * mm, "radius": 6 * mm});
            skLineSegment(sketch, "E86", {"start": v(-80, 0) * mm, "end": v(80, 0) * mm, "construction": true});
            skLineSegment(sketch, "E87.MirrorCS", {"start": v(-27.73, -90) * mm, "end": v(-15, -102.73) * mm});
            skLineSegment(sketch, "E88.MirrorCS", {"start": v(-15, -102.73) * mm, "end": v(-15, -114.73) * mm});
            skArc(sketch, "E89.MirrorCS", {"start": v(0, -129.73) * mm, "mid": v(-10.6, -125.33) * mm, "end": v(-15, -114.73) * mm});
            skArc(sketch, "E90.MirrorCS", {"start": v(14.73, -114.73) * mm, "mid": v(10.43, -125.24) * mm, "end": v(0, -129.73) * mm});
            skLineSegment(sketch, "E91.MirrorCS", {"start": v(14.73, -102.73) * mm, "end": v(14.73, -114.73) * mm});
            skLineSegment(sketch, "E92.MirrorCS", {"start": v(27.46, -90) * mm, "end": v(14.73, -102.73) * mm});
            skCircle(sketch, "E93.MirrorC", {"center": v(0, -114.73) * mm, "radius": 6 * mm});
            skSolve(sketch);
        }
        {
            var Q0;
            {var subQ1=sQuery(id+"F16.wireOp",EDGE,"E79");Q0=makeQuery(id+"F16.imprint","IMPRINT",FACE,{"disambiguationData":[TD([[makeQuery(id+"F16.imprint","IMPRINT",EDGE,{"derivedFrom":subQ1}),1.0]])]});}
            var Q1;
            Q1=makeQuery(id+"F16.imprint","IMPRINT",FACE,{"disambiguationData":[TD([[makeQuery(id+"F16.imprint","IMPRINT",EDGE,{"derivedFrom":makeQuery(id+"F1.opExtrude","CAP_EDGE",EDGE,{"disambiguationData":[OSD([sQuery(id+"F0.wireOp",EDGE,"E1.left")])],"isStart":true})}),-1.0]])]});
            var Q2;
            {var subQ0=sQuery(id+"F16.wireOp",EDGE,"E87.MirrorCS");Q2=makeQuery(id+"F16.imprint","IMPRINT",FACE,{"disambiguationData":[TD([[makeQuery(id+"F16.imprint","IMPRINT",EDGE,{"derivedFrom":subQ0}),1.0]])]});}
            var Q3;
            Q3=makeQuery(id+"F2.opExtrude","CAP_FACE",FACE,{"disambiguationData":[OSD([sQuery(id+"F0.wireOp",EDGE,"E12"),sQuery(id+"F0.wireOp",EDGE,"E13"),sQuery(id+"F0.wireOp",EDGE,"E14"),sQuery(id+"F0.wireOp",EDGE,"E15"),sQuery(id+"F0.wireOp",EDGE,"E17.filletArc"),sQuery(id+"F0.wireOp",EDGE,"E18.filletArc"),sQuery(id+"F0.wireOp",EDGE,"E19.filletArc"),sQuery(id+"F0.wireOp",EDGE,"E20.filletArc"),sQuery(id+"F0.wireOp",EDGE,"E25.0"),sQuery(id+"F0.wireOp",EDGE,"E25.1"),sQuery(id+"F0.wireOp",EDGE,"E25.2"),sQuery(id+"F0.wireOp",EDGE,"E25.3"),sQuery(id+"F0.wireOp",EDGE,"E25.4"),sQuery(id+"F0.wireOp",EDGE,"E25.5"),sQuery(id+"F0.wireOp",EDGE,"E25.6"),sQuery(id+"F0.wireOp",EDGE,"E25.7")])],"isStart":false});
            extrude(context, id + "F17", {"entities" : qUnion([Q0, Q1, Q2]), "endBound" : BoundingType.UP_TO_SURFACE, "depth" : 25 * mm, "endBoundEntityFace" : qUnion([Q3]), "offsetDistance" : 25 * mm});
        }
    });
